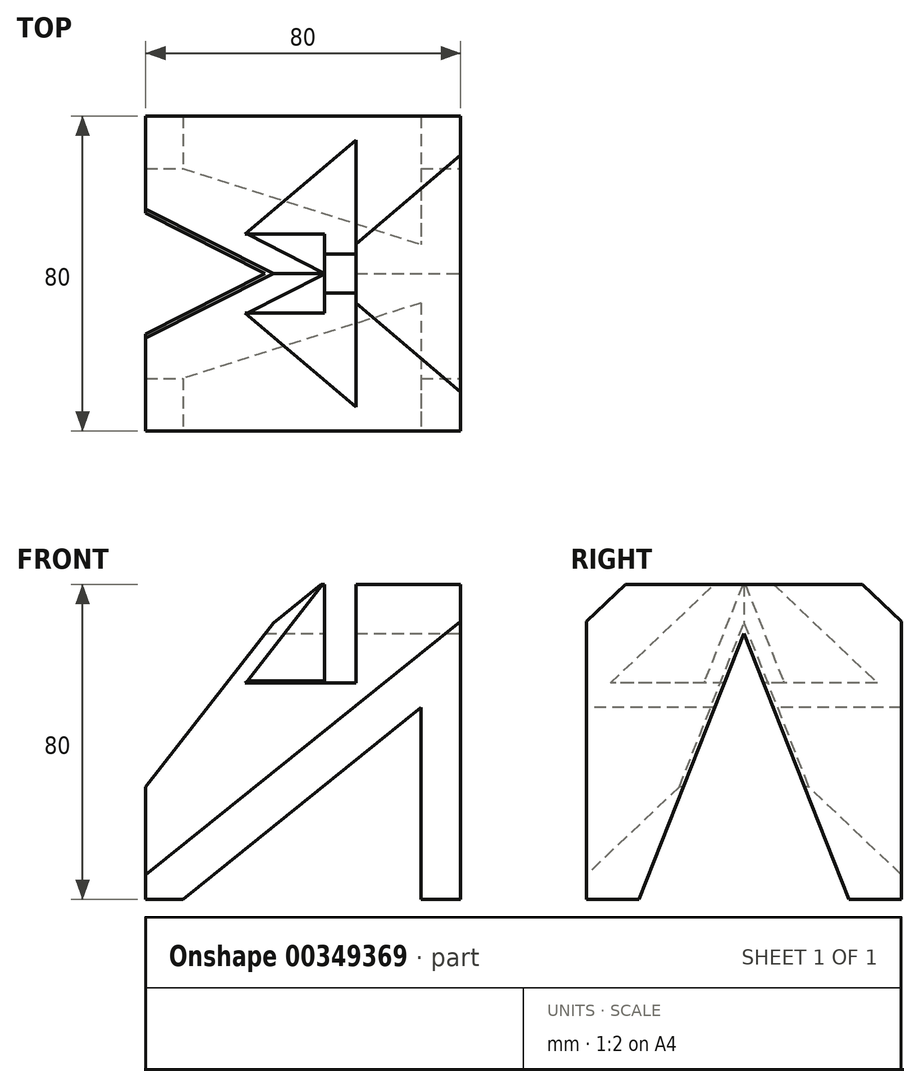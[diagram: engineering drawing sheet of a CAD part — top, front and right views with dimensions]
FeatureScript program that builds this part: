
annotation { "Feature Type Name" : "Feature", "Feature Type Description" : "" }
export const myFeature = defineFeature(function(context is Context, id is Id, definition is map)
    precondition{}
    {
        {
            var Q0;
            Q0=qCreatedBy(makeId("Top.planeOp"),FACE);
            var sketch = newSketch(context, id + "F0", { "sketchPlane" : qUnion([Q0])});
            skLineSegment(sketch, "E0.bottom", {"start": v(40, 40) * mm, "end": v(-40, 40) * mm});
            skLineSegment(sketch, "E0.top", {"start": v(40, -40) * mm, "end": v(-40, -40) * mm});
            skLineSegment(sketch, "E0.left", {"start": v(40, 40) * mm, "end": v(40, -40) * mm});
            skLineSegment(sketch, "E0.right", {"start": v(-40, 40) * mm, "end": v(-40, -40) * mm});
            skPoint(sketch, "E0.middle", {"position": v(0, 0) * mm});
            skSolve(sketch);
        }
        {
            var Q0;
            Q0=makeQuery(id+"F0.imprint","IMPRINT",FACE,{"disambiguationData":[TD([[makeQuery(id+"F0.imprint","IMPRINT",EDGE,{"derivedFrom":sQuery(id+"F0.wireOp",EDGE,"E0.bottom")}),1.0]])]});
            extrude(context, id + "F1", {"entities" : qUnion([Q0]), "depth" : 80 * mm});
        }
        {
            var Q0;
            Q0=makeQuery(id+"F1.opExtrude","SWEPT_FACE",FACE,{"disambiguationData":[OSD([sQuery(id+"F0.wireOp",EDGE,"E0.top")])]});
            var sketch = newSketch(context, id + "F2", { "sketchPlane" : qUnion([Q0])});
            skLineSegment(sketch, "E1", {"start": v(0, 80) * mm, "end": v(-40, 28.6) * mm});
            skLineSegment(sketch, "E2", {"start": v(-40, 28.6) * mm, "end": v(-40, 80) * mm});
            skLineSegment(sketch, "E3", {"start": v(-40, 80) * mm, "end": v(0, 80) * mm});
            skSolve(sketch);
        }
        {
            var Q0;
            Q0=makeQuery(id+"F2.imprint","IMPRINT",FACE,{"disambiguationData":[TD([[makeQuery(id+"F2.imprint","IMPRINT",EDGE,{"derivedFrom":sQuery(id+"F2.wireOp",EDGE,"E1")}),-1.0]])]});
            extrude(context, id + "F3", {"entities" : qUnion([Q0]), "operationType" : NewBodyOperationType.REMOVE, "oppositeDirection" : true, "depth" : 86.9 * mm});
        }
        {
            var Q0;
            Q0=makeQuery(id+"F1.opExtrude","CAP_FACE",FACE,{"disambiguationData":[OSD([sQuery(id+"F0.wireOp",EDGE,"E0.bottom"),sQuery(id+"F0.wireOp",EDGE,"E0.top"),sQuery(id+"F0.wireOp",EDGE,"E0.left"),sQuery(id+"F0.wireOp",EDGE,"E0.right")])],"isStart":false});
            var sketch = newSketch(context, id + "F4", { "sketchPlane" : qUnion([Q0])});
            skLineSegment(sketch, "E4.bottom", {"start": v(13.41, 44.64) * mm, "end": v(5.41, 44.64) * mm});
            skLineSegment(sketch, "E4.top", {"start": v(13.41, -44.64) * mm, "end": v(5.41, -44.64) * mm});
            skLineSegment(sketch, "E4.left", {"start": v(13.41, 44.64) * mm, "end": v(13.41, -44.64) * mm});
            skLineSegment(sketch, "E4.right", {"start": v(5.41, 44.64) * mm, "end": v(5.41, -44.64) * mm});
            skPoint(sketch, "E4.middle", {"position": v(9.41, 0) * mm});
            skSolve(sketch);
        }
        {
            var Q0;
            {var subQ0=sQuery(id+"F4.wireOp",EDGE,"E4.left");var subQ1=makeQuery(id+"F1.opExtrude","CAP_EDGE",EDGE,{"disambiguationData":[OSD([sQuery(id+"F0.wireOp",EDGE,"E0.bottom")])],"isStart":false});var subQ2=makeQuery(id+"F4.imprint","INTERSECT",VERTEX,{"derivedFrom":[subQ1,subQ0]});Q0=makeQuery(id+"F4.imprint","IMPRINT",FACE,{"disambiguationData":[TD([[makeQuery(id+"F4.imprint","IMPRINT",EDGE,{"disambiguationData":[TD([[subQ2,-1.0]])],"derivedFrom":subQ0}),-1.0]])]});}
            extrude(context, id + "F5", {"entities" : qUnion([Q0]), "operationType" : NewBodyOperationType.REMOVE, "oppositeDirection" : true, "depth" : 25 * mm});
        }
        {
            var Q0;
            Q0=makeQuery(id+"F5.boolean.opBoolean","COPY",FACE,{"derivedFrom":makeQuery(id+"F5.opExtrude","SWEPT_FACE",FACE,{"disambiguationData":[OSD([sQuery(id+"F4.wireOp",EDGE,"E4.right")])]})});
            var sketch = newSketch(context, id + "F6", { "sketchPlane" : qUnion([Q0])});
            skLineSegment(sketch, "E5.bottom", {"start": v(-40, 80) * mm, "end": v(-10, 80) * mm});
            skLineSegment(sketch, "E5.top", {"start": v(-40, 55) * mm, "end": v(-10, 55) * mm});
            skLineSegment(sketch, "E5.left", {"start": v(-40, 80) * mm, "end": v(-40, 55) * mm});
            skLineSegment(sketch, "E5.right", {"start": v(-10, 80) * mm, "end": v(-10, 55) * mm});
            skLineSegment(sketch, "E6.MirrorCS", {"start": v(40, 80) * mm, "end": v(10, 80) * mm});
            skLineSegment(sketch, "E7.MirrorCS", {"start": v(10, 80) * mm, "end": v(10, 55) * mm});
            skLineSegment(sketch, "E8.MirrorCS", {"start": v(40, 80) * mm, "end": v(40, 55) * mm});
            skLineSegment(sketch, "E9.MirrorCS", {"start": v(40, 55) * mm, "end": v(10, 55) * mm});
            skSolve(sketch);
        }
        {
            var Q0;
            Q0 = qSketchRegion(id + "F6", true);
            extrude(context, id + "F7", {"entities" : qUnion([Q0]), "operationType" : NewBodyOperationType.REMOVE, "oppositeDirection" : true, "depth" : 25 * mm});
        }
        {
            var Q0;
            Q0=makeQuery(id+"F1.opExtrude","SWEPT_FACE",FACE,{"disambiguationData":[OSD([sQuery(id+"F0.wireOp",EDGE,"E0.right")])]});
            var sketch = newSketch(context, id + "F8", { "sketchPlane" : qUnion([Q0])});
            skLineSegment(sketch, "E10", {"start": v(0, 80.8) * mm, "end": v(-10.17, 55.03) * mm});
            skLineSegment(sketch, "E11", {"start": v(-10.17, 55.03) * mm, "end": v(-61.05, 55.03) * mm});
            skLineSegment(sketch, "E12", {"start": v(-61.05, 55.03) * mm, "end": v(-61.05, 88.96) * mm});
            skLineSegment(sketch, "E13", {"start": v(-61.05, 88.96) * mm, "end": v(0, 88.96) * mm});
            skLineSegment(sketch, "E14.MirrorCS", {"start": v(0, 80.8) * mm, "end": v(10.17, 55.03) * mm});
            skLineSegment(sketch, "E15.MirrorCS", {"start": v(10.17, 55.03) * mm, "end": v(61.05, 55.03) * mm});
            skLineSegment(sketch, "E16.MirrorCS", {"start": v(61.05, 55.03) * mm, "end": v(61.05, 88.96) * mm});
            skLineSegment(sketch, "E17.MirrorCS", {"start": v(61.05, 88.96) * mm, "end": v(0, 88.96) * mm});
            skSolve(sketch);
        }
        {
            var Q0;
            Q0=makeQuery(id+"F8.imprint","IMPRINT",FACE,{"disambiguationData":[TD([[makeQuery(id+"F8.imprint","IMPRINT",EDGE,{"derivedFrom":sQuery(id+"F8.wireOp",EDGE,"E10")}),-1.0]])]});
            extrude(context, id + "F9", {"entities" : qUnion([Q0]), "operationType" : NewBodyOperationType.REMOVE, "oppositeDirection" : true, "depth" : 50.3 * mm});
        }
        {
            var Q0;
            Q0=makeQuery(id+"F9.boolean.opBoolean","INTERSECT",EDGE,{"derivedFrom":[makeQuery(id+"F3.boolean.opBoolean","COPY",FACE,{"derivedFrom":makeQuery(id+"F3.opExtrude","SWEPT_FACE",FACE,{"disambiguationData":[OSD([sQuery(id+"F2.wireOp",EDGE,"E1")])]})}),makeQuery(id+"F9.opExtrude","SWEPT_FACE",FACE,{"disambiguationData":[OSD([sQuery(id+"F8.wireOp",EDGE,"E10")])]})]});
            var Q1;
            Q1=makeQuery(id+"F9.boolean.opBoolean","INTERSECT",EDGE,{"derivedFrom":[makeQuery(id+"F3.boolean.opBoolean","COPY",FACE,{"derivedFrom":makeQuery(id+"F3.opExtrude","SWEPT_FACE",FACE,{"disambiguationData":[OSD([sQuery(id+"F2.wireOp",EDGE,"E1")])]})}),makeQuery(id+"F9.opExtrude","SWEPT_FACE",FACE,{"disambiguationData":[OSD([sQuery(id+"F8.wireOp",EDGE,"E14.MirrorCS")])]})]});
            chamfer(context, id + "F10", {"entities" : qUnion([Q0, Q1]), "width" : 5 * mm, "tangentPropagation" : true});
        }
        {
            var Q0;
            Q0=makeQuery(id+"F10.opChamfer","BLEND_FACE",FACE,{"disambiguationData":[OSD([sQuery(id+"F2.wireOp",EDGE,"E1"),sQuery(id+"F8.wireOp",EDGE,"E14.MirrorCS")])]});
            var sketch = newSketch(context, id + "F11", { "sketchPlane" : qUnion([Q0])});
            skLineSegment(sketch, "E18.bottom", {"start": v(139.77, -109.21) * mm, "end": v(-83.98, -109.21) * mm});
            skLineSegment(sketch, "E18.top", {"start": v(139.77, 122.65) * mm, "end": v(-83.98, 122.65) * mm});
            skLineSegment(sketch, "E18.left", {"start": v(139.77, -109.21) * mm, "end": v(139.77, 122.65) * mm});
            skLineSegment(sketch, "E18.right", {"start": v(-83.98, -109.21) * mm, "end": v(-83.98, 122.65) * mm});
            skSolve(sketch);
        }
        {
            var Q0;
            Q0=makeQuery(id+"F11.imprint","IMPRINT",FACE,{"disambiguationData":[TD([[makeQuery(id+"F11.imprint","IMPRINT",EDGE,{"derivedFrom":sQuery(id+"F11.wireOp",EDGE,"E18.bottom")}),-1.0]])]});
            extrude(context, id + "F12", {"entities" : qUnion([Q0]), "operationType" : NewBodyOperationType.REMOVE, "depth" : 25 * mm});
        }
        {
            var Q0;
            Q0=makeQuery(id+"F10.opChamfer","BLEND_FACE",FACE,{"disambiguationData":[OSD([sQuery(id+"F2.wireOp",EDGE,"E1"),sQuery(id+"F8.wireOp",EDGE,"E10")])]});
            var sketch = newSketch(context, id + "F13", { "sketchPlane" : qUnion([Q0])});
            skLineSegment(sketch, "E19.bottom", {"start": v(112.5, 124.59) * mm, "end": v(-94.71, 124.59) * mm});
            skLineSegment(sketch, "E19.top", {"start": v(112.5, -137.55) * mm, "end": v(-94.71, -137.55) * mm});
            skLineSegment(sketch, "E19.left", {"start": v(112.5, 124.59) * mm, "end": v(112.5, -137.55) * mm});
            skLineSegment(sketch, "E19.right", {"start": v(-94.71, 124.59) * mm, "end": v(-94.71, -137.55) * mm});
            skSolve(sketch);
        }
        {
            var Q0;
            Q0=makeQuery(id+"F13.imprint","IMPRINT",FACE,{"disambiguationData":[TD([[makeQuery(id+"F13.imprint","IMPRINT",EDGE,{"derivedFrom":sQuery(id+"F13.wireOp",EDGE,"E19.bottom")}),1.0]])]});
            extrude(context, id + "F14", {"entities" : qUnion([Q0]), "operationType" : NewBodyOperationType.REMOVE, "depth" : 25 * mm});
        }
        {
            var Q0;
            Q0=makeQuery(id+"F1.opExtrude","SWEPT_FACE",FACE,{"disambiguationData":[OSD([sQuery(id+"F0.wireOp",EDGE,"E0.top")])]});
            var sketch = newSketch(context, id + "F15", { "sketchPlane" : qUnion([Q0])});
            skLineSegment(sketch, "E20.0", {"start": v(30, 48.71) * mm, "end": v(30, 0) * mm});
            skLineSegment(sketch, "E20.1", {"start": v(30, 48.71) * mm, "end": v(-33.73, -2.55) * mm});
            skSolve(sketch);
        }
        {
            var Q0;
            {var subQ0=sQuery(id+"F15.wireOp",EDGE,"E20.0");Q0=makeQuery(id+"F15.imprint","IMPRINT",FACE,{"disambiguationData":[TD([[makeQuery(id+"F15.imprint","IMPRINT",EDGE,{"derivedFrom":subQ0}),-1.0]])]});}
            extrude(context, id + "F16", {"entities" : qUnion([Q0]), "operationType" : NewBodyOperationType.REMOVE, "oppositeDirection" : true, "depth" : 127.5 * mm});
        }
        {
            var Q0;
            Q0=qCreatedBy(makeId("Right.planeOp"),FACE);
            var sketch = newSketch(context, id + "F17", { "sketchPlane" : qUnion([Q0])});
            skLineSegment(sketch, "E21.0", {"start": v(0, 67.53) * mm, "end": v(15.3, 28.78) * mm});
            skLineSegment(sketch, "E21.1", {"start": v(-15.32, 28.7) * mm, "end": v(0, 67.53) * mm});
            skLineSegment(sketch, "E22", {"start": v(15.3, 28.78) * mm, "end": v(26.65, 0) * mm});
            skLineSegment(sketch, "E23", {"start": v(-15.32, 28.7) * mm, "end": v(-26.65, 0) * mm});
            skLineSegment(sketch, "E24.0", {"start": v(15.36, 28.6) * mm, "end": v(-15.36, 28.6) * mm});
            skLineSegment(sketch, "E25", {"start": v(26.65, 0) * mm, "end": v(-26.65, 0) * mm});
            skSolve(sketch);
        }
        {
            var Q0;
            Q0 = qSketchRegion(id + "F17", true);
            extrude(context, id + "F18", {"entities" : qUnion([Q0]), "operationType" : NewBodyOperationType.REMOVE, "endBound" : BoundingType.THROUGH_ALL, "oppositeDirection" : true, "depth" : 25 * mm, "hasSecondDirection" : true, "secondDirectionBound" : SecondDirectionBoundingType.THROUGH_ALL, "secondDirectionOppositeDirection" : false, "secondDirectionDepth" : 25 * mm});
        }
    });
